# Revit family: TV-106_RFA
name_source: partatom
category: Aparatos sanitarios
units: mm (PartAtom-declared; Revit-internal decimal feet)

## family parameters
Compartido = Sí
Corte con vacíos al cargar = No
Cota de conector redondo = Diámetro de uso
Número OmniClass = 23.45.00.00
Punto de cálculo de habitación = Sí
Se basa en plano de trabajo = Sí
Siempre vertical = Sí
Tipo de pieza = Normal
Título OmniClass = Sanitary, Laundry, and Cleaning Equipment

## types (1)
- TV-106
    Accessories = Economizador para autoajuste de flujo y palanca con recubrimiento antibacterial
    Chrome = Brass Chromed
    Comentarios de tipo = Llave Economizadora
    Connection = ½" - 14 NPSM
    Descripción = Llave Economizadora con Seguro Antirrobo
    Elevación por Defecto = 3"
    Elevación por defecto = 41"
    Fabricante = HELVEX S.A. DE C.V.
    Imagen de tipo = TV-106.jpg
    Max. Water Flow = 0.8 gal/min
    Max. Working Pressure = 85.3 psi
    Min. Working Pressure = 3.6 psi
    Modelo = TV-106
    Operation = Cierre Automático y Perilla multidireccional
    Total Height = 7"
    Total Length = 8"
    Total Width = 2"
    URL = https://www.helvex.com.mx

## geometry (parser evidence)
native form markers: Sweep x3
no freeform markers — native parametric forms only
